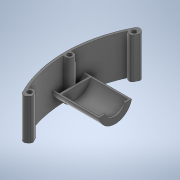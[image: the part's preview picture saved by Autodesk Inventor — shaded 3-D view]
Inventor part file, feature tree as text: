
AUTODESK INVENTOR PART (.ipt)
format: ipt  version: 2020 (Build 240168000, 168)  size: 1,135,104 bytes
history: native  units: mm
features: extrude x17, projected_geometry x13, sketch x8, other x4, fillet x2
ambient origin geometry x8: Origin, YZ Plane, XZ Plane, XY Plane, X Axis, Y Axis, Z Axis, Center Point
bodies: Body1 (feature_tree)
feature tree (44):
  other  "Твердое тело1"
  extrude  "outer"  TaperAngle=45.0deg  [1 undecoded]
  extrude  "inner"  Depth=7.0mm
  extrude  "Выдавливание3"  Depth=20.0mm
  extrude  "Выдавливание4"  Depth=7.0mm
  extrude  "Выдавливание5"  Depth=3.2mm
  extrude  "Выдавливание6"  Depth=59.0mm
  extrude  "Выдавливание7"  Depth=83.0mm
  extrude  "Выдавливание8"  Depth=69.0mm
  sketch  "Эскиз6"
  extrude  "Выдавливание9"  Depth=55.0mm
  extrude  "Выдавливание10"  Depth=3.0mm
  fillet  "Сопряжение1"  Radius=8.0mm
  other  "РабПлоскость2"
  sketch  "Эскиз8"
  extrude  "Выдавливание11"  Depth=5.0mm
  fillet  "Сопряжение2"  Radius=2.0mm
  sketch  "3D эскиз1"
  other  "РабПлоскость4"
  sketch  "Эскиз11"
  extrude  "Выдавливание12"  Depth=40.0mm TaperAngle=360.0deg
  extrude  "Выдавливание13"  Depth=2.0mm
  extrude  "Выдавливание14"  Depth=105.0mm
  extrude  "Выдавливание15"  Depth=2.0mm
  extrude  "Выдавливание16"  Depth=2.0mm TaperAngle=0.0deg
  extrude  "Выдавливание17"  Depth=3.5mm
  sketch  "Эскиз1"
  sketch  "Эскиз2"
  projected_geometry  "Спроецированная петля1"
  projected_geometry  "Спроецированная петля2"
  projected_geometry  "Спроецированная петля3"
  projected_geometry  "Спроецированная петля4"
  projected_geometry  "Спроецированная петля5"
  projected_geometry  "Спроецированная петля8"
  projected_geometry  "Спроецированная петля9"
  projected_geometry  "Спроецированная петля10"
  other  "Проецирование на поверхность1"
  projected_geometry  "Спроецированная петля14"
  projected_geometry  "Спроецированная петля15"
  projected_geometry  "Спроецированная петля16"
  sketch  "Эскиз12"
  projected_geometry  "Спроецированная петля17"
  sketch  "Эскиз13"
  projected_geometry  "Спроецированная петля18"
note: 1 required parameter value undecoded (feature->parameter linkage not recoverable at this tier; creation-order binding heuristic only, values carry confidence <= 0.55)
